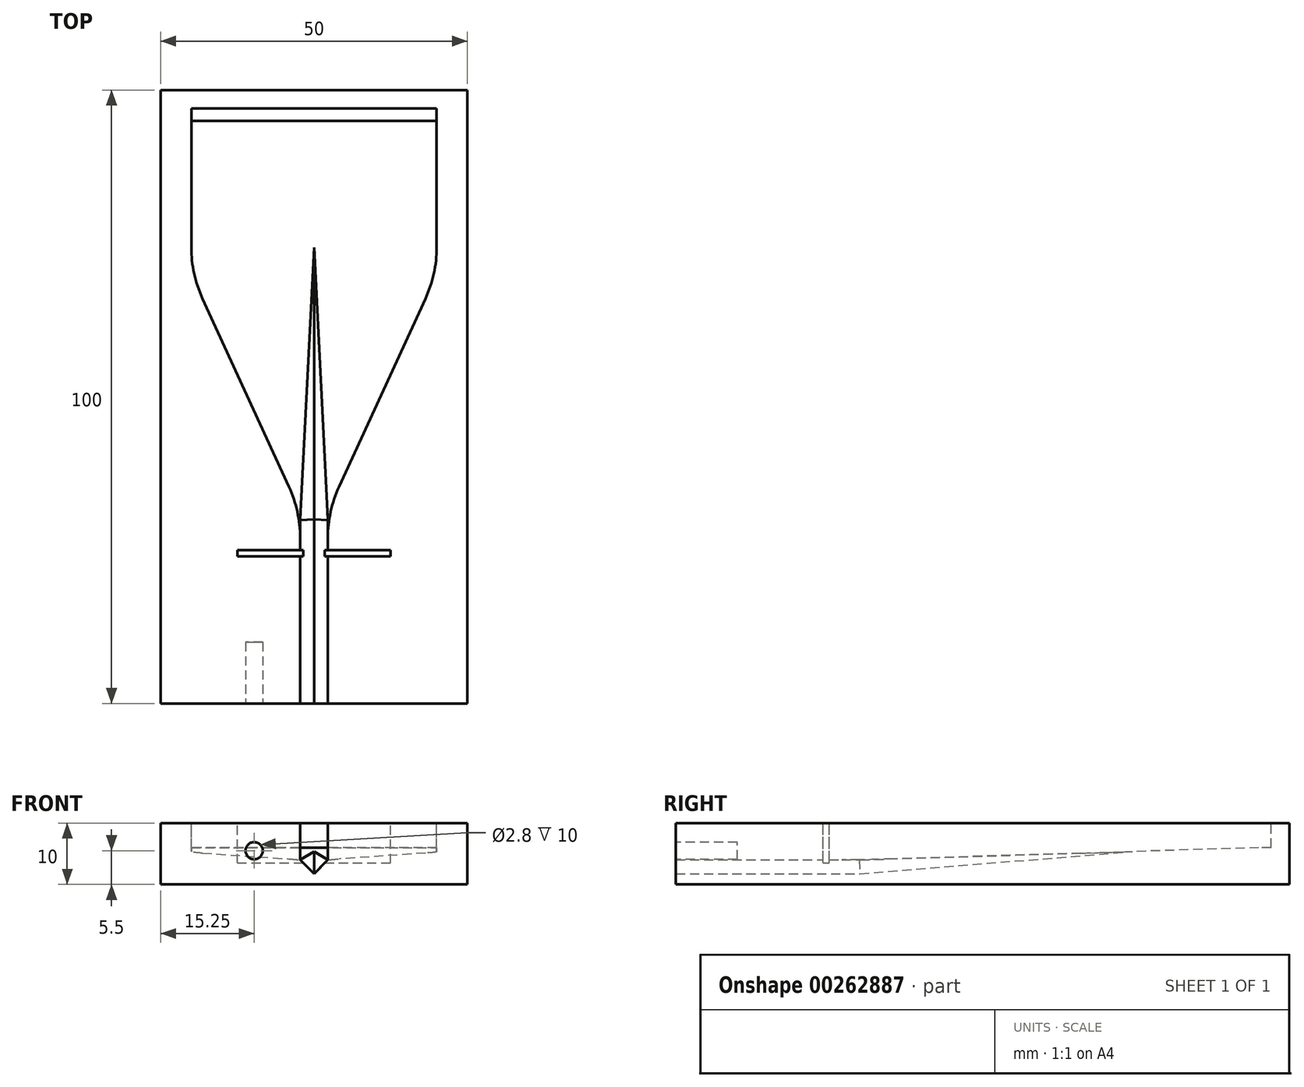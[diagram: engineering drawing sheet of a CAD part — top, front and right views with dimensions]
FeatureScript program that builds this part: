
annotation { "Feature Type Name" : "Feature", "Feature Type Description" : "" }
export const myFeature = defineFeature(function(context is Context, id is Id, definition is map)
    precondition{}
    {
        {
            var Q0;
            Q0=qCreatedBy(makeId("Top.planeOp"),FACE);
            var sketch = newSketch(context, id + "F0", { "sketchPlane" : qUnion([Q0])});
            skLineSegment(sketch, "E0.bottom", {"start": v(-25, 50) * mm, "end": v(25, 50) * mm});
            skLineSegment(sketch, "E0.top", {"start": v(-25, -50) * mm, "end": v(25, -50) * mm});
            skLineSegment(sketch, "E0.left", {"start": v(-25, 50) * mm, "end": v(-25, -50) * mm});
            skLineSegment(sketch, "E0.right", {"start": v(25, 50) * mm, "end": v(25, -50) * mm});
            skPoint(sketch, "E0.middle", {"position": v(0, 0) * mm});
            skSolve(sketch);
        }
        {
            var Q0;
            Q0 = qSketchRegion(id + "F0", true);
            extrude(context, id + "F1", {"entities" : qUnion([Q0]), "depth" : 10 * mm});
        }
        {
            var Q0;
            Q0=makeQuery(id+"F1.opExtrude","CAP_FACE",FACE,{"disambiguationData":[OSD([sQuery(id+"F0.wireOp",EDGE,"E0.bottom"),sQuery(id+"F0.wireOp",EDGE,"E0.top"),sQuery(id+"F0.wireOp",EDGE,"E0.left"),sQuery(id+"F0.wireOp",EDGE,"E0.right")])],"isStart":false});
            var sketch = newSketch(context, id + "F2", { "sketchPlane" : qUnion([Q0])});
            skLineSegment(sketch, "E1", {"start": v(-20, 50) * mm, "end": v(-20, 24.38) * mm});
            skLineSegment(sketch, "E2", {"start": v(-18.17, 16.02) * mm, "end": v(-4.08, -14.65) * mm});
            skLineSegment(sketch, "E3", {"start": v(-2.25, -23) * mm, "end": v(-2.25, -50) * mm});
            skPoint(sketch, "E4.visualSharp", {"position": v(-20, 20) * mm});
            skArc(sketch, "E4.filletArc", {"start": v(-20, 24.38) * mm, "mid": v(-19.54, 20.1) * mm, "end": v(-18.17, 16.02) * mm});
            skPoint(sketch, "E5.visualSharp", {"position": v(-2.25, -18.62) * mm});
            skArc(sketch, "E5.filletArc", {"start": v(-2.25, -23) * mm, "mid": v(-2.71, -18.73) * mm, "end": v(-4.08, -14.65) * mm});
            skLineSegment(sketch, "E6.MirrorCS", {"start": v(20, 50) * mm, "end": v(20, 24.38) * mm});
            skArc(sketch, "E7.MirrorCS", {"start": v(20, 24.38) * mm, "mid": v(19.54, 20.1) * mm, "end": v(18.17, 16.02) * mm});
            skLineSegment(sketch, "E8.MirrorCS", {"start": v(18.17, 16.02) * mm, "end": v(4.08, -14.65) * mm});
            skArc(sketch, "E9.MirrorCS", {"start": v(2.25, -23) * mm, "mid": v(2.71, -18.73) * mm, "end": v(4.08, -14.65) * mm});
            skLineSegment(sketch, "E10.MirrorCS", {"start": v(2.25, -23) * mm, "end": v(2.25, -50) * mm});
            skLineSegment(sketch, "E11", {"start": v(-20, 47) * mm, "end": v(20, 47) * mm});
            skSolve(sketch);
        }
        {
            var Q0;
            Q0=makeQuery(id+"F2.imprint","IMPRINT",FACE,{"disambiguationData":[TD([[makeQuery(id+"F2.imprint","IMPRINT",EDGE,{"derivedFrom":sQuery(id+"F2.wireOp",EDGE,"E2")}),1.0]])]});
            extrude(context, id + "F3", {"entities" : qUnion([Q0]), "operationType" : NewBodyOperationType.REMOVE, "oppositeDirection" : true, "depth" : 8 * mm});
        }
        {
            var Q0;
            Q0=makeQuery(id+"F1.opExtrude","SWEPT_FACE",FACE,{"disambiguationData":[OSD([sQuery(id+"F0.wireOp",EDGE,"E0.left")])]});
            var sketch = newSketch(context, id + "F4", { "sketchPlane" : qUnion([Q0])});
            skLineSegment(sketch, "E12", {"start": v(-50, 6) * mm, "end": v(-45, 6) * mm});
            skLineSegment(sketch, "E13", {"start": v(-45, 6) * mm, "end": v(20, 4) * mm});
            skLineSegment(sketch, "E14", {"start": v(-50, 6) * mm, "end": v(-50, 0) * mm});
            skLineSegment(sketch, "E15", {"start": v(-50, 0) * mm, "end": v(50, 0) * mm});
            skLineSegment(sketch, "E16", {"start": v(50, 0) * mm, "end": v(50, 2) * mm});
            skLineSegment(sketch, "E17", {"start": v(50, 4) * mm, "end": v(20, 4) * mm});
            skSolve(sketch);
        }
        {
            var Q0;
            Q0=makeQuery(id+"F4.imprint","IMPRINT",FACE,{"disambiguationData":[TD([[makeQuery(id+"F4.imprint","IMPRINT",EDGE,{"derivedFrom":sQuery(id+"F4.wireOp",EDGE,"E12")}),-1.0]])]});
            var Q1;
            Q1=makeQuery(id+"F1.opExtrude","SWEPT_FACE",FACE,{"disambiguationData":[OSD([sQuery(id+"F0.wireOp",EDGE,"E0.right")])]});
            extrude(context, id + "F5", {"entities" : qUnion([Q0]), "operationType" : NewBodyOperationType.ADD, "endBound" : BoundingType.UP_TO_SURFACE, "oppositeDirection" : true, "endBoundEntityFace" : qUnion([Q1]), "depth" : 25 * mm});
        }
        {
            var Q0;
            {var subQ0=sQuery(id+"F0.wireOp",EDGE,"E0.top");Q0=makeQuery(id+"F5.boolean.opBoolean","MERGE",FACE,{"derivedFrom":[makeQuery(id+"F1.opExtrude","SWEPT_FACE",FACE,{"disambiguationData":[OSD([subQ0])]}),makeQuery(id+"F5.opExtrude","SWEPT_FACE",FACE,{"disambiguationData":[OSD([subQ0,sQuery(id+"F0.wireOp",EDGE,"E0.left"),sQuery(id+"F4.wireOp",EDGE,"E16")])]})]});}
            var sketch = newSketch(context, id + "F6", { "sketchPlane" : qUnion([Q0])});
            skLineSegment(sketch, "E18", {"start": v(-2.25, 4) * mm, "end": v(2.25, 4) * mm});
            skLineSegment(sketch, "E19", {"start": v(2.25, 4) * mm, "end": v(0, 1.75) * mm});
            skLineSegment(sketch, "E20", {"start": v(0, 1.75) * mm, "end": v(-2.25, 4) * mm});
            skSolve(sketch);
        }
        {
            var Q0;
            Q0=qCreatedBy(makeId("Right.planeOp"),FACE);
            var sketch = newSketch(context, id + "F7", { "sketchPlane" : qUnion([Q0])});
            skPoint(sketch, "E21.0", {"position": v(-50, 1.75) * mm});
            skPoint(sketch, "E22.0", {"position": v(24.38, 5.37) * mm});
            skLineSegment(sketch, "E23", {"start": v(-50, 1.75) * mm, "end": v(-20, 1.75) * mm});
            skLineSegment(sketch, "E24", {"start": v(-20, 1.75) * mm, "end": v(24.38, 5.37) * mm});
            skPoint(sketch, "E25.0", {"position": v(-20, 4) * mm});
            skSolve(sketch);
        }
        {
            var Q0;
            Q0=makeQuery(id+"F6.imprint","IMPRINT",FACE,{"disambiguationData":[TD([[makeQuery(id+"F6.imprint","IMPRINT",EDGE,{"derivedFrom":sQuery(id+"F6.wireOp",EDGE,"E18")}),1.0]])]});
            var Q1;
            Q1=sQuery(id+"F7.wireOp",EDGE,"E23");
            var Q2;
            Q2=sQuery(id+"F7.wireOp",EDGE,"E24");
            sweep(context, id + "F8", {"operationType" : NewBodyOperationType.REMOVE, "profiles" : qUnion([Q0]), "path" : qUnion([Q1, Q2])});
        }
        {
            var Q0;
            Q0=makeQuery(id+"F1.opExtrude","CAP_FACE",FACE,{"disambiguationData":[OSD([sQuery(id+"F0.wireOp",EDGE,"E0.bottom"),sQuery(id+"F0.wireOp",EDGE,"E0.top"),sQuery(id+"F0.wireOp",EDGE,"E0.left"),sQuery(id+"F0.wireOp",EDGE,"E0.right")])],"isStart":false});
            var sketch = newSketch(context, id + "F9", { "sketchPlane" : qUnion([Q0])});
            skLineSegment(sketch, "E26.bottom", {"start": v(-12.5, -25) * mm, "end": v(12.5, -25) * mm});
            skLineSegment(sketch, "E26.top", {"start": v(-12.5, -26) * mm, "end": v(12.5, -26) * mm});
            skLineSegment(sketch, "E26.left", {"start": v(-12.5, -25) * mm, "end": v(-12.5, -26) * mm});
            skLineSegment(sketch, "E26.right", {"start": v(12.5, -25) * mm, "end": v(12.5, -26) * mm});
            skPoint(sketch, "E26.middle", {"position": v(0, -25.5) * mm});
            skSolve(sketch);
        }
        {
            var Q0;
            Q0 = qSketchRegion(id + "F9", true);
            extrude(context, id + "F10", {"entities" : qUnion([Q0]), "operationType" : NewBodyOperationType.REMOVE, "oppositeDirection" : true, "depth" : 6.5 * mm});
        }
        {
            var Q0;
            {var subQ0=sQuery(id+"F0.wireOp",EDGE,"E0.top");Q0=makeQuery(id+"F5.boolean.opBoolean","MERGE",FACE,{"derivedFrom":[makeQuery(id+"F1.opExtrude","SWEPT_FACE",FACE,{"disambiguationData":[OSD([subQ0])]}),makeQuery(id+"F5.opExtrude","SWEPT_FACE",FACE,{"disambiguationData":[OSD([subQ0,sQuery(id+"F0.wireOp",EDGE,"E0.left"),sQuery(id+"F4.wireOp",EDGE,"E16")])]})]});}
            var sketch = newSketch(context, id + "F11", { "sketchPlane" : qUnion([Q0])});
            skCircle(sketch, "E27", {"center": v(-9.75, 5.5) * mm, "radius": 1.4 * mm});
            skSolve(sketch);
        }
        {
            var Q0;
            Q0=makeQuery(id+"F11.imprint","IMPRINT",FACE,{"disambiguationData":[TD([[makeQuery(id+"F11.imprint","IMPRINT",EDGE,{"derivedFrom":sQuery(id+"F11.wireOp",EDGE,"E27")}),1.0]])]});
            extrude(context, id + "F12", {"entities" : qUnion([Q0]), "operationType" : NewBodyOperationType.REMOVE, "oppositeDirection" : true, "depth" : 10 * mm});
        }
    });
